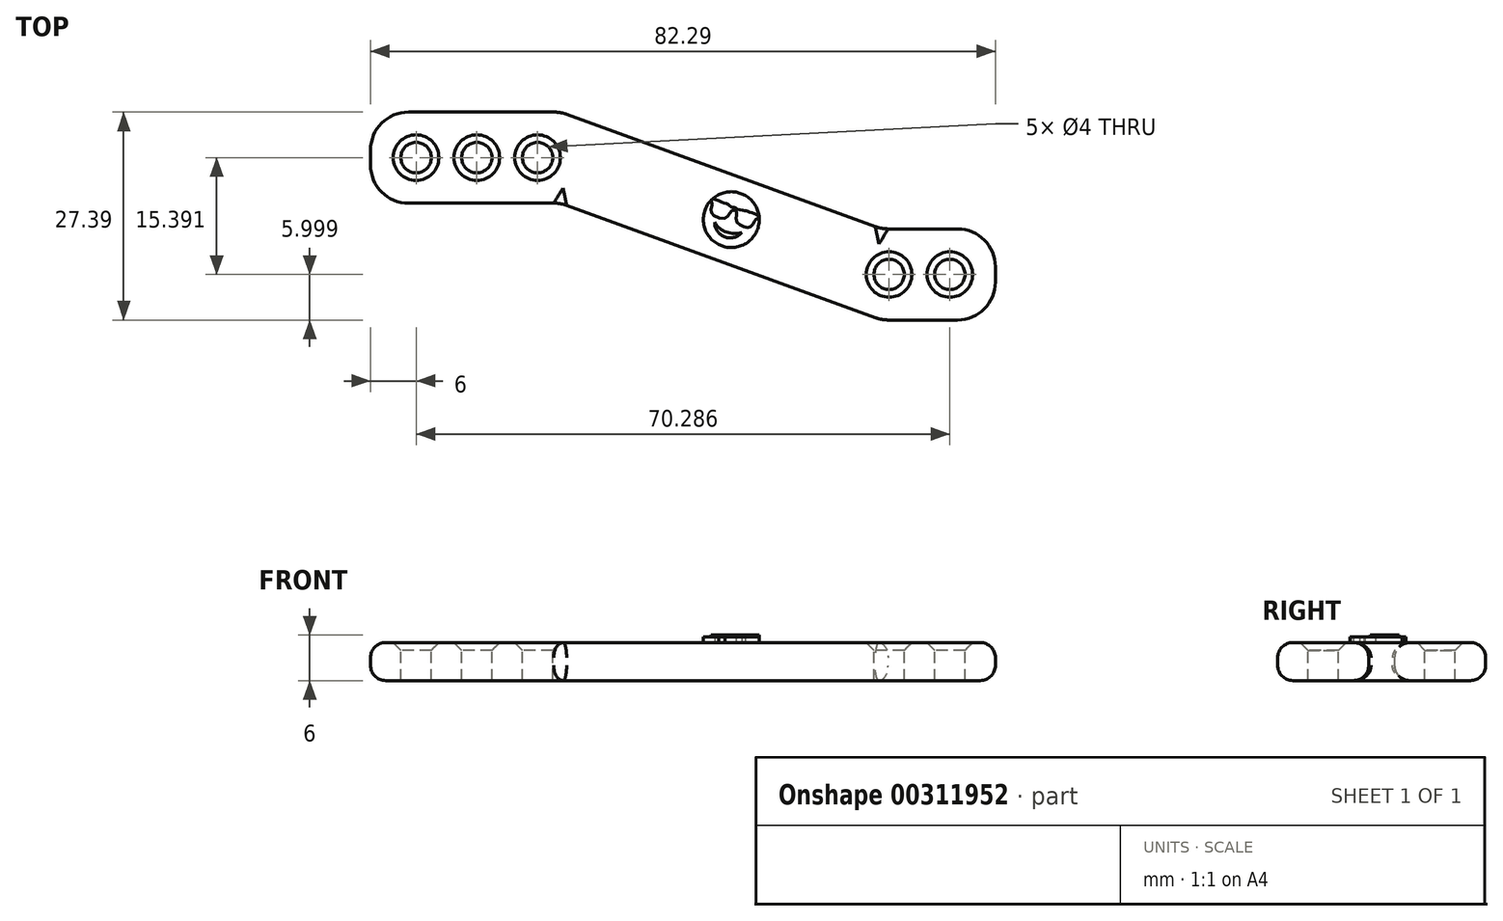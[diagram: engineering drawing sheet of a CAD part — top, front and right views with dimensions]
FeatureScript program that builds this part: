
annotation { "Feature Type Name" : "Feature", "Feature Type Description" : "" }
export const myFeature = defineFeature(function(context is Context, id is Id, definition is map)
    precondition{}
    {
        {
            var Q0;
            Q0=qCreatedBy(makeId("Top.planeOp"),FACE);
            var sketch = newSketch(context, id + "F0", { "sketchPlane" : qUnion([Q0])});
            skLineSegment(sketch, "E0.bottom", {"start": v(0, 12) * mm, "end": v(25, 12) * mm});
            skLineSegment(sketch, "E0.top", {"start": v(0, 0) * mm, "end": v(25, 0) * mm});
            skLineSegment(sketch, "E0.left", {"start": v(0, 12) * mm, "end": v(0, 0) * mm});
            skLineSegment(sketch, "E0.right", {"start": v(25, 12) * mm, "end": v(25, 0) * mm});
            skLineSegment(sketch, "E1.bottom", {"start": v(67.29, -3.4) * mm, "end": v(82.29, -3.4) * mm});
            skLineSegment(sketch, "E1.top", {"start": v(67.29, -15.4) * mm, "end": v(82.29, -15.4) * mm});
            skLineSegment(sketch, "E1.left", {"start": v(67.29, -3.4) * mm, "end": v(67.29, -15.4) * mm});
            skLineSegment(sketch, "E1.right", {"start": v(82.29, -3.4) * mm, "end": v(82.29, -15.4) * mm});
            skLineSegment(sketch, "E2", {"start": v(25, 12) * mm, "end": v(67.29, -3.4) * mm});
            skLineSegment(sketch, "E3", {"start": v(25, 0) * mm, "end": v(67.29, -15.4) * mm});
            skSolve(sketch);
        }
        {
            var Q0;
            Q0=makeQuery(id+"F0.imprint","IMPRINT",FACE,{"disambiguationData":[TD([[makeQuery(id+"F0.imprint","IMPRINT",EDGE,{"derivedFrom":sQuery(id+"F0.wireOp",EDGE,"E0.bottom")}),-1.0]])]});
            var Q1;
            Q1=makeQuery(id+"F0.imprint","IMPRINT",FACE,{"disambiguationData":[TD([[makeQuery(id+"F0.imprint","IMPRINT",EDGE,{"derivedFrom":sQuery(id+"F0.wireOp",EDGE,"E0.right")}),1.0]])]});
            var Q2;
            Q2=makeQuery(id+"F0.imprint","IMPRINT",FACE,{"disambiguationData":[TD([[makeQuery(id+"F0.imprint","IMPRINT",EDGE,{"derivedFrom":sQuery(id+"F0.wireOp",EDGE,"E1.bottom")}),-1.0]])]});
            extrude(context, id + "F1", {"entities" : qUnion([Q0, Q1, Q2]), "depth" : 5 * mm});
        }
        {
            var Q0;
            Q0=makeQuery(id+"F1.opExtrude","CAP_FACE",FACE,{"disambiguationData":[OSD([sQuery(id+"F0.wireOp",EDGE,"E0.bottom"),sQuery(id+"F0.wireOp",EDGE,"E0.top"),sQuery(id+"F0.wireOp",EDGE,"E0.left"),sQuery(id+"F0.wireOp",EDGE,"E1.bottom"),sQuery(id+"F0.wireOp",EDGE,"E1.top"),sQuery(id+"F0.wireOp",EDGE,"E1.right"),sQuery(id+"F0.wireOp",EDGE,"E2"),sQuery(id+"F0.wireOp",EDGE,"E3")])],"isStart":false});
            var sketch = newSketch(context, id + "F2", { "sketchPlane" : qUnion([Q0])});
            skCircle(sketch, "E4", {"center": v(6, 6) * mm, "radius": 2 * mm});
            skCircle(sketch, "E5", {"center": v(76.29, -9.4) * mm, "radius": 2 * mm});
            skCircle(sketch, "E6.1.0.0", {"center": v(14, 6) * mm, "radius": 2 * mm});
            skCircle(sketch, "E6.2.0.0", {"center": v(22, 6) * mm, "radius": 2 * mm});
            skLineSegment(sketch, "E6.direction1", {"start": v(6, 6) * mm, "end": v(14, 6) * mm, "construction": true});
            skCircle(sketch, "E7.1.0.0", {"center": v(68.29, -9.4) * mm, "radius": 2 * mm});
            skLineSegment(sketch, "E7.direction1", {"start": v(76.29, -9.4) * mm, "end": v(68.29, -9.4) * mm, "construction": true});
            skSolve(sketch);
        }
        {
            var Q0;
            Q0 = qSketchRegion(id + "F2", true);
            extrude(context, id + "F3", {"entities" : qUnion([Q0]), "operationType" : NewBodyOperationType.REMOVE, "endBound" : BoundingType.THROUGH_ALL, "oppositeDirection" : true, "depth" : 5 * mm});
        }
        {
            var Q0;
            Q0=makeQuery(id+"F1.opExtrude","CAP_EDGE",EDGE,{"disambiguationData":[OSD([sQuery(id+"F0.wireOp",EDGE,"E3")])],"isStart":false});
            var Q1;
            Q1=makeQuery(id+"F1.opExtrude","CAP_EDGE",EDGE,{"disambiguationData":[OSD([sQuery(id+"F0.wireOp",EDGE,"E1.top")])],"isStart":false});
            var Q2;
            Q2=makeQuery(id+"F1.opExtrude","CAP_EDGE",EDGE,{"disambiguationData":[OSD([sQuery(id+"F0.wireOp",EDGE,"E1.right")])],"isStart":false});
            var Q3;
            Q3=makeQuery(id+"F1.opExtrude","CAP_EDGE",EDGE,{"disambiguationData":[OSD([sQuery(id+"F0.wireOp",EDGE,"E1.bottom")])],"isStart":false});
            var Q4;
            Q4=makeQuery(id+"F1.opExtrude","CAP_EDGE",EDGE,{"disambiguationData":[OSD([sQuery(id+"F0.wireOp",EDGE,"E2")])],"isStart":false});
            var Q5;
            Q5=makeQuery(id+"F1.opExtrude","CAP_EDGE",EDGE,{"disambiguationData":[OSD([sQuery(id+"F0.wireOp",EDGE,"E0.bottom")])],"isStart":false});
            var Q6;
            Q6=makeQuery(id+"F1.opExtrude","CAP_EDGE",EDGE,{"disambiguationData":[OSD([sQuery(id+"F0.wireOp",EDGE,"E0.left")])],"isStart":false});
            var Q7;
            Q7=makeQuery(id+"F1.opExtrude","CAP_EDGE",EDGE,{"disambiguationData":[OSD([sQuery(id+"F0.wireOp",EDGE,"E0.top")])],"isStart":false});
            var Q8;
            Q8=makeQuery(id+"F1.opExtrude","CAP_EDGE",EDGE,{"disambiguationData":[OSD([sQuery(id+"F0.wireOp",EDGE,"E3")])],"isStart":true});
            var Q9;
            Q9=makeQuery(id+"F1.opExtrude","CAP_EDGE",EDGE,{"disambiguationData":[OSD([sQuery(id+"F0.wireOp",EDGE,"E1.top")])],"isStart":true});
            var Q10;
            Q10=makeQuery(id+"F1.opExtrude","CAP_EDGE",EDGE,{"disambiguationData":[OSD([sQuery(id+"F0.wireOp",EDGE,"E1.right")])],"isStart":true});
            var Q11;
            Q11=makeQuery(id+"F1.opExtrude","CAP_EDGE",EDGE,{"disambiguationData":[OSD([sQuery(id+"F0.wireOp",EDGE,"E1.bottom")])],"isStart":true});
            var Q12;
            Q12=makeQuery(id+"F1.opExtrude","CAP_EDGE",EDGE,{"disambiguationData":[OSD([sQuery(id+"F0.wireOp",EDGE,"E2")])],"isStart":true});
            var Q13;
            Q13=makeQuery(id+"F1.opExtrude","CAP_EDGE",EDGE,{"disambiguationData":[OSD([sQuery(id+"F0.wireOp",EDGE,"E0.bottom")])],"isStart":true});
            var Q14;
            Q14=makeQuery(id+"F1.opExtrude","CAP_EDGE",EDGE,{"disambiguationData":[OSD([sQuery(id+"F0.wireOp",EDGE,"E0.left")])],"isStart":true});
            var Q15;
            Q15=makeQuery(id+"F1.opExtrude","CAP_EDGE",EDGE,{"disambiguationData":[OSD([sQuery(id+"F0.wireOp",EDGE,"E0.top")])],"isStart":true});
            fillet(context, id + "F4", {"entities" : qUnion([Q0, Q1, Q2, Q3, Q4, Q5, Q6, Q7, Q8, Q9, Q10, Q11, Q12, Q13, Q14, Q15]), "radius" : 2 * mm, "tangentPropagation" : true, "allowEdgeOverflow" : false});
        }
        {
            var Q0;
            Q0=makeQuery(id+"F4.opFillet","BLEND_EDGE",EDGE,{"blendedFrom":[makeQuery(id+"F1.opExtrude","CAP_EDGE",EDGE,{"disambiguationData":[OSD([sQuery(id+"F0.wireOp",EDGE,"E0.top")])],"isStart":false}),makeQuery(id+"F1.opExtrude","CAP_EDGE",EDGE,{"disambiguationData":[OSD([sQuery(id+"F0.wireOp",EDGE,"E0.left")])],"isStart":false})],"blendedInto":[]});
            var Q1;
            Q1=makeQuery(id+"F4.opFillet","BLEND_EDGE",EDGE,{"blendedFrom":[makeQuery(id+"F1.opExtrude","CAP_EDGE",EDGE,{"disambiguationData":[OSD([sQuery(id+"F0.wireOp",EDGE,"E0.top")])],"isStart":false}),makeQuery(id+"F1.opExtrude","CAP_EDGE",EDGE,{"disambiguationData":[OSD([sQuery(id+"F0.wireOp",EDGE,"E3")])],"isStart":false})],"blendedInto":[]});
            var Q2;
            Q2=makeQuery(id+"F4.opFillet","BLEND_EDGE",EDGE,{"blendedFrom":[makeQuery(id+"F1.opExtrude","CAP_EDGE",EDGE,{"disambiguationData":[OSD([sQuery(id+"F0.wireOp",EDGE,"E1.top")])],"isStart":false}),makeQuery(id+"F1.opExtrude","CAP_EDGE",EDGE,{"disambiguationData":[OSD([sQuery(id+"F0.wireOp",EDGE,"E3")])],"isStart":false})],"blendedInto":[]});
            var Q3;
            Q3=makeQuery(id+"F4.opFillet","BLEND_EDGE",EDGE,{"blendedFrom":[makeQuery(id+"F1.opExtrude","CAP_EDGE",EDGE,{"disambiguationData":[OSD([sQuery(id+"F0.wireOp",EDGE,"E1.top")])],"isStart":false}),makeQuery(id+"F1.opExtrude","CAP_EDGE",EDGE,{"disambiguationData":[OSD([sQuery(id+"F0.wireOp",EDGE,"E1.right")])],"isStart":false})],"blendedInto":[]});
            var Q4;
            Q4=makeQuery(id+"F4.opFillet","BLEND_EDGE",EDGE,{"blendedFrom":[makeQuery(id+"F1.opExtrude","CAP_EDGE",EDGE,{"disambiguationData":[OSD([sQuery(id+"F0.wireOp",EDGE,"E1.bottom")])],"isStart":false}),makeQuery(id+"F1.opExtrude","CAP_EDGE",EDGE,{"disambiguationData":[OSD([sQuery(id+"F0.wireOp",EDGE,"E1.right")])],"isStart":false})],"blendedInto":[]});
            var Q5;
            Q5=makeQuery(id+"F4.opFillet","BLEND_EDGE",EDGE,{"blendedFrom":[makeQuery(id+"F1.opExtrude","CAP_EDGE",EDGE,{"disambiguationData":[OSD([sQuery(id+"F0.wireOp",EDGE,"E1.bottom")])],"isStart":false}),makeQuery(id+"F1.opExtrude","CAP_EDGE",EDGE,{"disambiguationData":[OSD([sQuery(id+"F0.wireOp",EDGE,"E2")])],"isStart":false})],"blendedInto":[]});
            var Q6;
            Q6=makeQuery(id+"F4.opFillet","BLEND_EDGE",EDGE,{"blendedFrom":[makeQuery(id+"F1.opExtrude","CAP_EDGE",EDGE,{"disambiguationData":[OSD([sQuery(id+"F0.wireOp",EDGE,"E0.bottom")])],"isStart":false}),makeQuery(id+"F1.opExtrude","CAP_EDGE",EDGE,{"disambiguationData":[OSD([sQuery(id+"F0.wireOp",EDGE,"E2")])],"isStart":false})],"blendedInto":[]});
            var Q7;
            Q7=makeQuery(id+"F4.opFillet","BLEND_EDGE",EDGE,{"blendedFrom":[makeQuery(id+"F1.opExtrude","CAP_EDGE",EDGE,{"disambiguationData":[OSD([sQuery(id+"F0.wireOp",EDGE,"E0.bottom")])],"isStart":false}),makeQuery(id+"F1.opExtrude","CAP_EDGE",EDGE,{"disambiguationData":[OSD([sQuery(id+"F0.wireOp",EDGE,"E0.left")])],"isStart":false})],"blendedInto":[]});
            fillet(context, id + "F5", {"entities" : qUnion([Q0, Q1, Q2, Q3, Q4, Q5, Q6, Q7]), "radius" : 5 * mm, "tangentPropagation" : true, "allowEdgeOverflow" : false});
        }
        {
            var Q0;
            Q0=makeQuery(id+"F1.opExtrude","CAP_FACE",FACE,{"disambiguationData":[OSD([sQuery(id+"F0.wireOp",EDGE,"E0.bottom"),sQuery(id+"F0.wireOp",EDGE,"E0.top"),sQuery(id+"F0.wireOp",EDGE,"E0.left"),sQuery(id+"F0.wireOp",EDGE,"E1.bottom"),sQuery(id+"F0.wireOp",EDGE,"E1.top"),sQuery(id+"F0.wireOp",EDGE,"E1.right"),sQuery(id+"F0.wireOp",EDGE,"E2"),sQuery(id+"F0.wireOp",EDGE,"E3")])],"isStart":false});
            chamfer(context, id + "F6", {"entities" : qUnion([Q0]), "width" : 1 * mm, "tangentPropagation" : true});
        }
        {
            var Q0;
            Q0=makeQuery(id+"F1.opExtrude","CAP_FACE",FACE,{"disambiguationData":[OSD([sQuery(id+"F0.wireOp",EDGE,"E0.bottom"),sQuery(id+"F0.wireOp",EDGE,"E0.top"),sQuery(id+"F0.wireOp",EDGE,"E0.left"),sQuery(id+"F0.wireOp",EDGE,"E1.bottom"),sQuery(id+"F0.wireOp",EDGE,"E1.top"),sQuery(id+"F0.wireOp",EDGE,"E1.right"),sQuery(id+"F0.wireOp",EDGE,"E2"),sQuery(id+"F0.wireOp",EDGE,"E3")])],"isStart":false});
            var sketch = newSketch(context, id + "F7", { "sketchPlane" : qUnion([Q0])});
            skCircle(sketch, "E8", {"center": v(47.5, -2.18) * mm, "radius": 3.68 * mm});
            skFitSpline(sketch, "E9", {"points": [v(45.07, 0.59) * mm, v(46.42, 0.1) * mm, v(47.2, -0.24) * mm, v(47.49, -0.48) * mm, v(47.9, -0.59) * mm, v(48.17, -0.7) * mm, v(48.33, -0.81) * mm, v(49.26, -0.97) * mm, v(49.58, -1.06) * mm, v(50.28, -1.27) * mm, v(51.15, -1.68) * mm], "startDerivative": vector(8.96, -3.28) * mm, "endDerivative": vector(6.68, -3.56) * mm});
            skLineSegment(sketch, "E10", {"start": v(45.07, 0.59) * mm, "end": v(44.85, 0.27) * mm});
            skLineSegment(sketch, "E11", {"start": v(51.15, -1.68) * mm, "end": v(51.1, -1.98) * mm});
            skPoint(sketch, "E12.1.internal.snap0", {"position": v(44.96, 0.43) * mm});
            skPoint(sketch, "E12.2.internal.snap0", {"position": v(44.96, 0.43) * mm});
            skFitSpline(sketch, "E12", {"points": [v(44.85, 0.27) * mm, v(44.96, 0.02) * mm, v(44.96, -0.2) * mm, v(44.85, -0.94) * mm, v(45.06, -1.48) * mm, v(46.5, -2.01) * mm, v(47.22, -1.5) * mm, v(47.51, -1.04) * mm, v(47.86, -0.92) * mm, v(48.2, -1.14) * mm, v(48.15, -1.68) * mm, v(48.2, -2.46) * mm, v(48.9, -2.99) * mm, v(49.68, -3.2) * mm, v(50.11, -3.06) * mm, v(50.52, -2.44) * mm, v(50.68, -2.18) * mm, v(51.1, -1.98) * mm], "startDerivative": vector(3.49, -6.62) * mm, "endDerivative": vector(9.78, 3.68) * mm});
            skArc(sketch, "E13", {"start": v(45.32, -2.53) * mm, "mid": v(46.63, -4.44) * mm, "end": v(48.88, -3.88) * mm});
            skArc(sketch, "E14", {"start": v(45.32, -2.53) * mm, "mid": v(46.87, -3.81) * mm, "end": v(48.88, -3.88) * mm});
            skSolve(sketch);
        }
        {
            var Q0;
            Q0=makeQuery(id+"F7.imprint","IMPRINT",FACE,{"disambiguationData":[TD([[makeQuery(id+"F7.imprint","IMPRINT",EDGE,{"derivedFrom":sQuery(id+"F7.wireOp",EDGE,"E9")}),-1.0]])]});
            extrude(context, id + "F8", {"entities" : qUnion([Q0]), "operationType" : NewBodyOperationType.ADD, "depth" : 1 * mm});
        }
        {
            var Q0;
            {var subQ0=sQuery(id+"F7.wireOp",EDGE,"E10");Q0=makeQuery(id+"F7.imprint","IMPRINT",FACE,{"disambiguationData":[TD([[makeQuery(id+"F7.imprint","IMPRINT",EDGE,{"derivedFrom":subQ0}),-1.0]])]});}
            var Q1;
            {var subQ0=sQuery(id+"F7.wireOp",EDGE,"E9");Q1=makeQuery(id+"F7.imprint","IMPRINT",FACE,{"disambiguationData":[TD([[makeQuery(id+"F7.imprint","IMPRINT",EDGE,{"derivedFrom":subQ0}),1.0]])]});}
            extrude(context, id + "F9", {"entities" : qUnion([Q0, Q1]), "operationType" : NewBodyOperationType.ADD, "depth" : 0.75 * mm});
        }
    });
